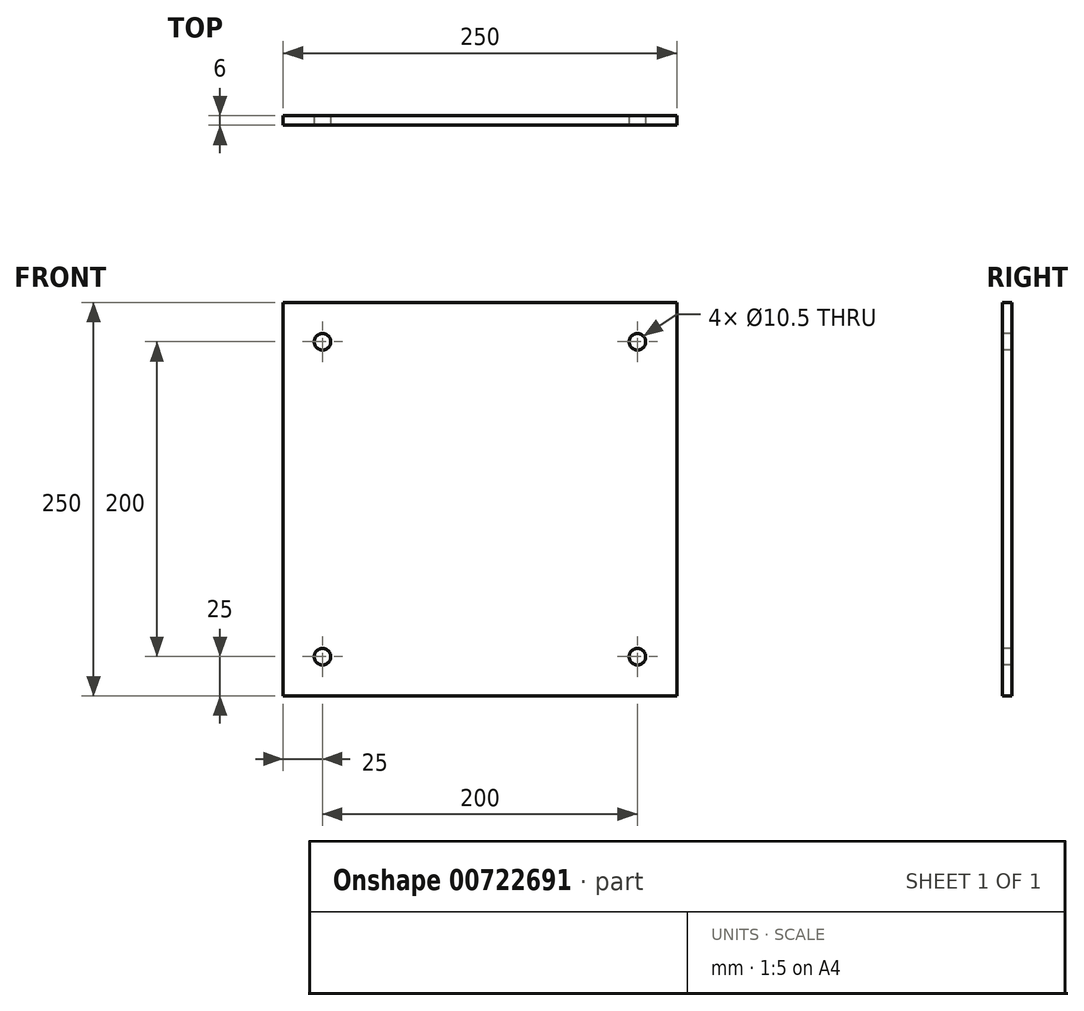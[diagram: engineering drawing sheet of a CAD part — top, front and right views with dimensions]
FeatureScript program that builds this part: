
annotation { "Feature Type Name" : "Feature", "Feature Type Description" : "" }
export const myFeature = defineFeature(function(context is Context, id is Id, definition is map)
    precondition{}
    {
        {
            var Q0;
            Q0=qCreatedBy(makeId("Front.planeOp"),FACE);
            var sketch = newSketch(context, id + "F0", { "sketchPlane" : qUnion([Q0])});
            skLineSegment(sketch, "E0.bottom", {"start": v(125, 125) * mm, "end": v(-125, 125) * mm});
            skLineSegment(sketch, "E0.top", {"start": v(125, -125) * mm, "end": v(-125, -125) * mm});
            skLineSegment(sketch, "E0.left", {"start": v(125, 125) * mm, "end": v(125, -125) * mm});
            skLineSegment(sketch, "E0.right", {"start": v(-125, 125) * mm, "end": v(-125, -125) * mm});
            skPoint(sketch, "E0.middle", {"position": v(0, 0) * mm});
            skLineSegment(sketch, "E1", {"start": v(0, 142.2) * mm, "end": v(0, -149.86) * mm, "construction": true});
            skLineSegment(sketch, "E2", {"start": v(-156.84, 0) * mm, "end": v(184.51, 0) * mm, "construction": true});
            skPoint(sketch, "E3", {"position": v(-100, 100) * mm});
            skPoint(sketch, "E4", {"position": v(100, 100) * mm});
            skPoint(sketch, "E5", {"position": v(100, -100) * mm});
            skPoint(sketch, "E6", {"position": v(-100, -100) * mm});
            skSolve(sketch);
        }
        {
            var Q0;
            Q0 = qSketchRegion(id + "F0", true);
            extrude(context, id + "F1", {"entities" : qUnion([Q0]), "depth" : 6 * mm, "offsetDistance" : 25 * mm});
        }
        {
            var Q0;
            Q0=sQuery(id+"F0.wireOp",VERTEX,"E5");
            var Q1;
            Q1=sQuery(id+"F0.wireOp",VERTEX,"E4");
            var Q2;
            Q2=sQuery(id+"F0.wireOp",VERTEX,"E3");
            var Q3;
            Q3=sQuery(id+"F0.wireOp",VERTEX,"E6");
            var Q4;
            Q4=makeQuery(id+"F1.opExtrude","SWEPT_BODY",BODY,{"disambiguationData":[OSD([sQuery(id+"F0.wireOp",EDGE,"E0.bottom"),sQuery(id+"F0.wireOp",EDGE,"E0.top"),sQuery(id+"F0.wireOp",EDGE,"E0.left"),sQuery(id+"F0.wireOp",EDGE,"E0.right")])]});
            hole(context, id + "F2", {"style" : HoleStyle.SIMPLE, "endStyle" : HoleEndStyle.THROUGH, "oppositeDirection" : true, "holeDiameter" : 10.5 * mm, "majorDiameter" : 5 * mm, "isTappedThrough" : true, "tappedDepth" : 12 * mm, "tapClearance" : 3, "locations" : qUnion([Q0, Q1, Q2, Q3]), "scope" : qUnion([Q4])});
        }
    });
